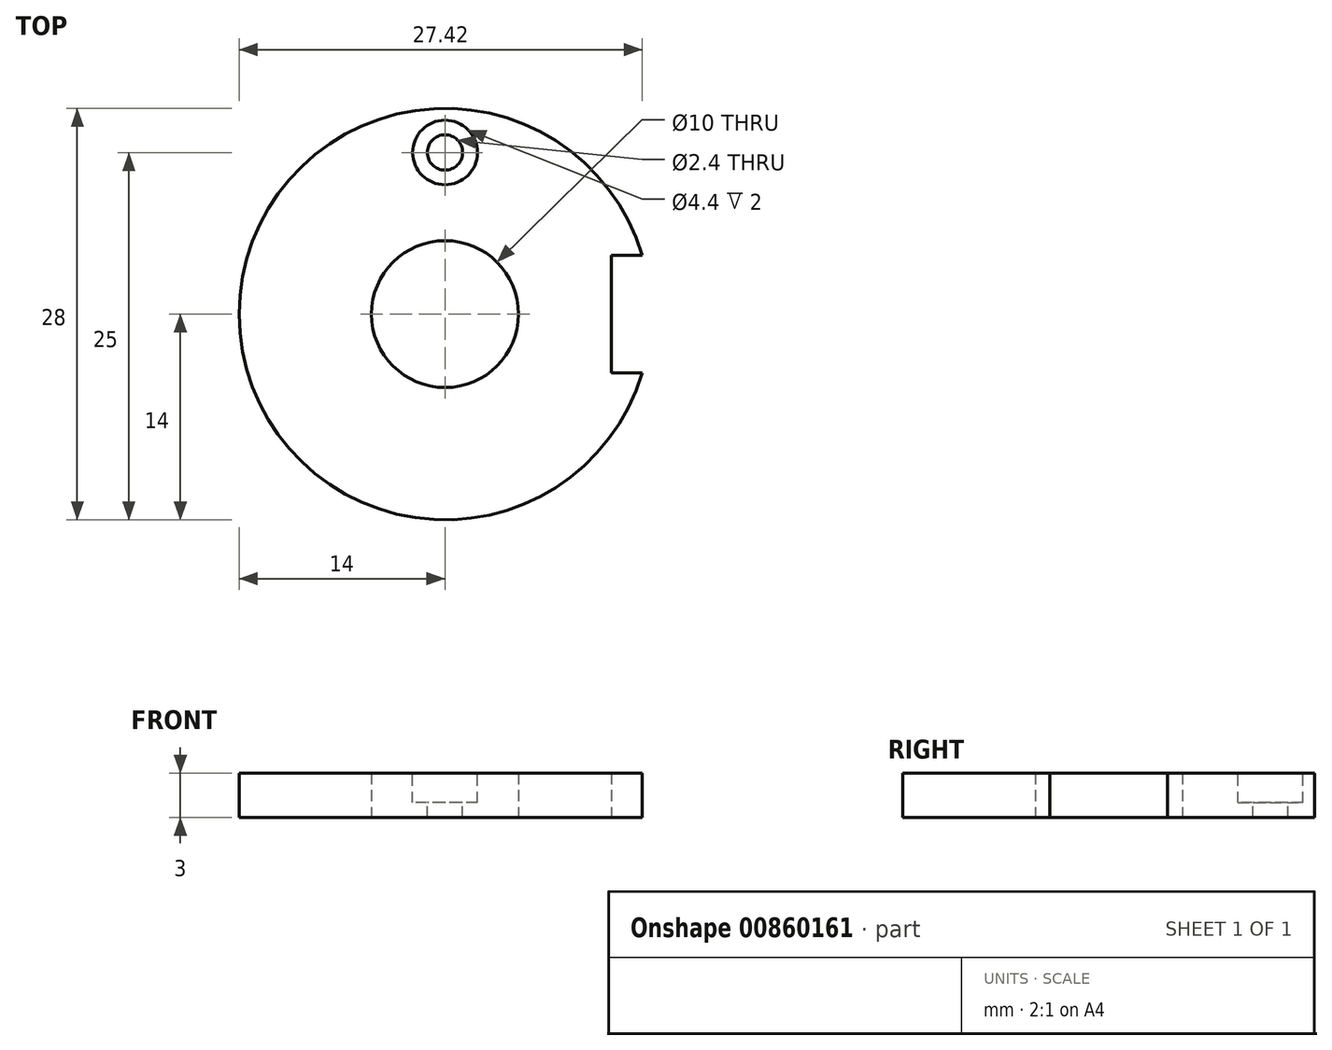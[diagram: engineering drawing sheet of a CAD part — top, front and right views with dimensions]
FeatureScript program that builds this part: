
annotation { "Feature Type Name" : "Feature", "Feature Type Description" : "" }
export const myFeature = defineFeature(function(context is Context, id is Id, definition is map)
    precondition{}
    {
        {
            var Q0;
            Q0=qCreatedBy(makeId("Top.planeOp"),FACE);
            var sketch = newSketch(context, id + "F0", { "sketchPlane" : qUnion([Q0])});
            skArc(sketch, "E0", {"start": v(13.42, 4) * mm, "mid": v(-14, 0) * mm, "end": v(13.42, -4) * mm});
            skLineSegment(sketch, "E1", {"start": v(13.42, 4) * mm, "end": v(11.3, 4) * mm});
            skLineSegment(sketch, "E2", {"start": v(11.3, 4) * mm, "end": v(11.3, -4) * mm});
            skLineSegment(sketch, "E3", {"start": v(11.3, -4) * mm, "end": v(13.42, -4) * mm});
            skCircle(sketch, "E4", {"center": v(0, 0) * mm, "radius": 5 * mm});
            skSolve(sketch);
        }
        {
            var Q0;
            Q0=makeQuery(id+"F0.imprint","IMPRINT",FACE,{"disambiguationData":[TD([[makeQuery(id+"F0.imprint","IMPRINT",EDGE,{"derivedFrom":sQuery(id+"F0.wireOp",EDGE,"E0")}),1.0]])]});
            extrude(context, id + "F1", {"entities" : qUnion([Q0]), "depth" : 3 * mm, "offsetDistance" : 25 * mm});
        }
        {
            var Q0;
            Q0=makeQuery(id+"F1.opExtrude","CAP_FACE",FACE,{"disambiguationData":[OSD([sQuery(id+"F0.wireOp",EDGE,"E0"),sQuery(id+"F0.wireOp",EDGE,"E1"),sQuery(id+"F0.wireOp",EDGE,"E2"),sQuery(id+"F0.wireOp",EDGE,"E3")])],"isStart":false});
            var sketch = newSketch(context, id + "F2", { "sketchPlane" : qUnion([Q0])});
            skPoint(sketch, "E5", {"position": v(0, 11) * mm});
            skSolve(sketch);
        }
        {
            var Q0;
            Q0=sQuery(id+"F2.wireOp",VERTEX,"E5");
            var Q1;
            Q1=makeQuery(id+"F1.opExtrude","SWEPT_BODY",BODY,{"disambiguationData":[OSD([sQuery(id+"F0.wireOp",EDGE,"E0"),sQuery(id+"F0.wireOp",EDGE,"E1"),sQuery(id+"F0.wireOp",EDGE,"E2"),sQuery(id+"F0.wireOp",EDGE,"E3")])]});
            hole(context, id + "F3", {"style" : HoleStyle.C_BORE, "endStyle" : HoleEndStyle.THROUGH, "holeDiameter" : 2.4 * mm, "cBoreDiameter" : 4.4 * mm, "cBoreDepth" : 2 * mm, "majorDiameter" : 3 * mm, "isTappedThrough" : true, "tappedDepth" : 5.5 * mm, "tapClearance" : 3, "startFromSketch" : true, "locations" : qUnion([Q0]), "scope" : qUnion([Q1])});
        }
    });
